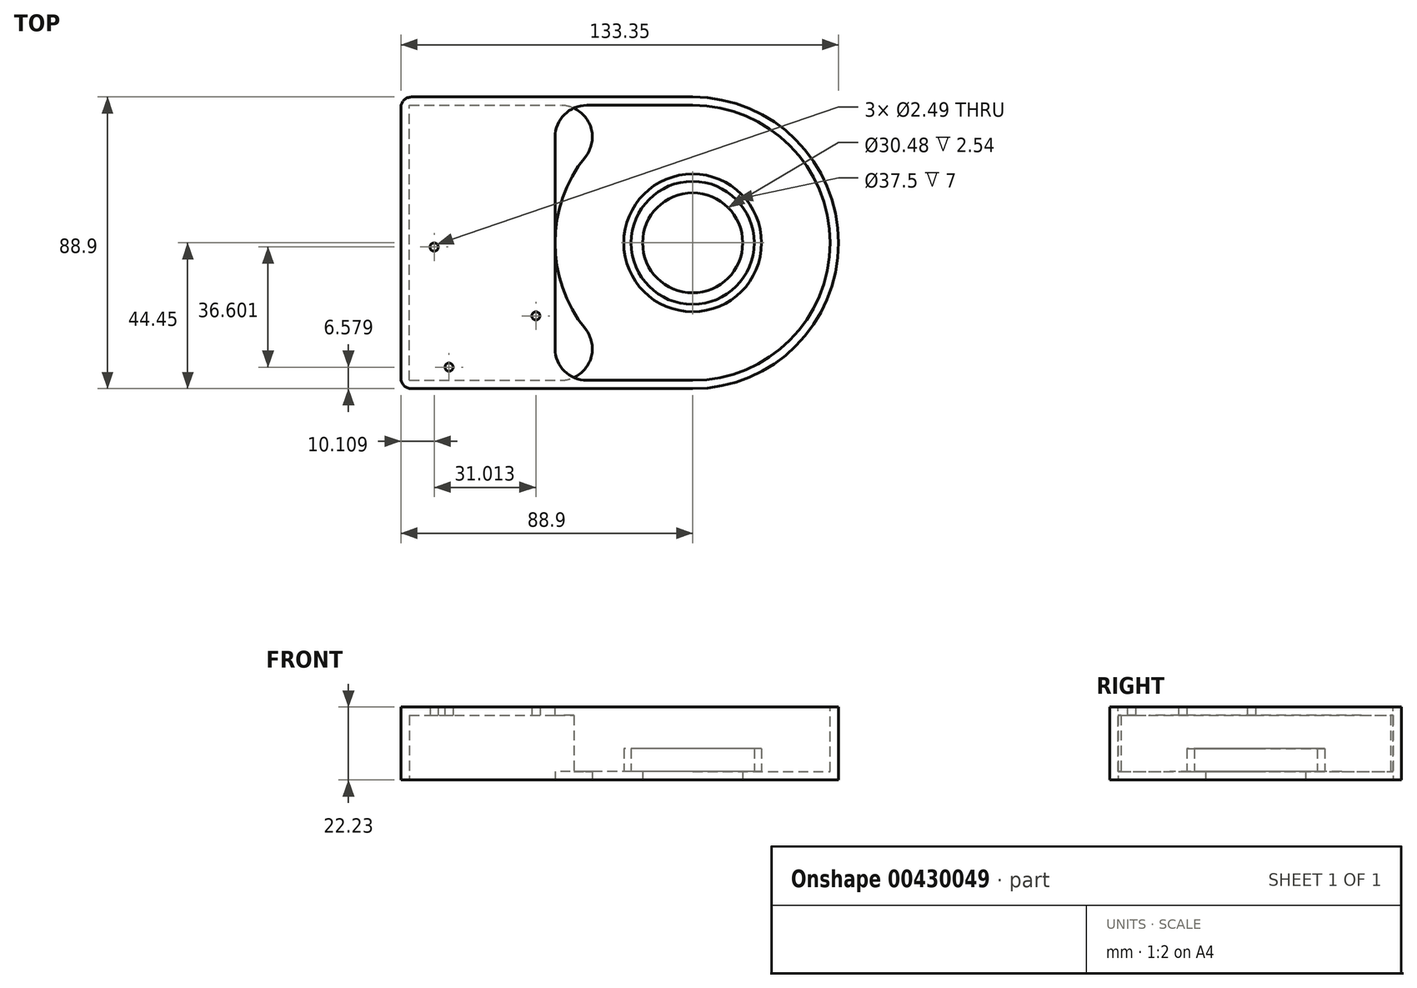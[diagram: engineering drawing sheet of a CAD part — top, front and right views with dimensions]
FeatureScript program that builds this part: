
annotation { "Feature Type Name" : "Feature", "Feature Type Description" : "" }
export const myFeature = defineFeature(function(context is Context, id is Id, definition is map)
    precondition{}
    {
        {
            var Q0;
            Q0=qCreatedBy(makeId("Top.planeOp"),FACE);
            var sketch = newSketch(context, id + "F0", { "sketchPlane" : qUnion([Q0])});
            skLineSegment(sketch, "E0.bottom", {"start": v(3.17, 0) * mm, "end": v(88.9, 0) * mm});
            skLineSegment(sketch, "E0.top", {"start": v(3.17, 88.9) * mm, "end": v(88.9, 88.9) * mm});
            skLineSegment(sketch, "E0.left", {"start": v(0, 3.17) * mm, "end": v(0, 85.73) * mm});
            skLineSegment(sketch, "E0.right", {"start": v(88.9, 0) * mm, "end": v(88.9, 88.9) * mm});
            skArc(sketch, "E1", {"start": v(88.9, 0) * mm, "mid": v(133.35, 44.45) * mm, "end": v(88.9, 88.9) * mm});
            skPoint(sketch, "E1.third.point", {"position": v(133.34, 45.55) * mm});
            skCircle(sketch, "E2", {"center": v(88.9, 44.45) * mm, "radius": 15.24 * mm});
            skPoint(sketch, "E3.visualSharp", {"position": v(0, 88.9) * mm});
            skArc(sketch, "E3.filletArc", {"start": v(3.17, 88.9) * mm, "mid": v(0.93, 87.97) * mm, "end": v(0, 85.73) * mm});
            skPoint(sketch, "E4.visualSharp", {"position": v(0, 0) * mm});
            skArc(sketch, "E4.filletArc", {"start": v(0, 3.17) * mm, "mid": v(0.93, 0.93) * mm, "end": v(3.17, 0) * mm});
            skSolve(sketch);
        }
        {
            var Q0;
            Q0=qSketchRegion(id+"F0",true);
            extrude(context, id + "F1", {"entities" : qUnion([Q0]), "depth" : 22.22 * mm});
        }
        {
            var Q0;
            Q0=makeQuery(id+"F1.opExtrude","CAP_FACE",FACE,{"disambiguationData":[OSD([sQuery(id+"F0.wireOp",EDGE,"E0.bottom"),sQuery(id+"F0.wireOp",EDGE,"E0.top"),sQuery(id+"F0.wireOp",EDGE,"E0.left"),sQuery(id+"F0.wireOp",EDGE,"E1"),sQuery(id+"F0.wireOp",EDGE,"E2")])],"isStart":false});
            var sketch = newSketch(context, id + "F2", { "sketchPlane" : qUnion([Q0])});
            skArc(sketch, "E5.0.0", {"start": v(88.9, 0) * mm, "mid": v(133.35, 44.45) * mm, "end": v(88.9, 88.9) * mm, "construction": true});
            skArc(sketch, "E6", {"start": v(88.9, 2.54) * mm, "mid": v(130.8, 44.45) * mm, "end": v(88.9, 86.36) * mm});
            skLineSegment(sketch, "E7.bottom", {"start": v(88.9, 86.36) * mm, "end": v(56.64, 86.36) * mm});
            skLineSegment(sketch, "E7.top", {"start": v(88.9, 2.54) * mm, "end": v(56.64, 2.54) * mm});
            skLineSegment(sketch, "E7.left", {"start": v(88.9, 86.36) * mm, "end": v(88.9, 2.54) * mm});
            skLineSegment(sketch, "E7.right", {"start": v(46.99, 76.7) * mm, "end": v(46.99, 12.2) * mm});
            skPoint(sketch, "E8.visualSharp", {"position": v(46.99, 86.36) * mm});
            skArc(sketch, "E8.filletArc", {"start": v(56.64, 86.36) * mm, "mid": v(49.82, 83.53) * mm, "end": v(46.99, 76.7) * mm});
            skPoint(sketch, "E9.visualSharp", {"position": v(47, 2.54) * mm});
            skArc(sketch, "E9.filletArc", {"start": v(46.99, 12.2) * mm, "mid": v(49.82, 5.37) * mm, "end": v(56.64, 2.54) * mm});
            skSolve(sketch);
        }
        {
            var Q0;
            Q0=qSketchRegion(id+"F2",true);
            extrude(context, id + "F3", {"entities" : qUnion([Q0]), "operationType" : NewBodyOperationType.REMOVE, "oppositeDirection" : true, "depth" : 19.68 * mm});
        }
        {
            var Q0;
            Q0=makeQuery(id+"F1.opExtrude","CAP_FACE",FACE,{"disambiguationData":[OSD([sQuery(id+"F0.wireOp",EDGE,"E0.bottom"),sQuery(id+"F0.wireOp",EDGE,"E0.top"),sQuery(id+"F0.wireOp",EDGE,"E0.left"),sQuery(id+"F0.wireOp",EDGE,"E1"),sQuery(id+"F0.wireOp",EDGE,"E2")])],"isStart":true});
            var sketch = newSketch(context, id + "F4", { "sketchPlane" : qUnion([Q0])});
            skArc(sketch, "E10", {"start": v(56.2, -18.23) * mm, "mid": v(46.99, -44.45) * mm, "end": v(56.2, -70.67) * mm});
            skLineSegment(sketch, "E11.0", {"start": v(2.54, -86.36) * mm, "end": v(48.67, -86.36) * mm});
            skLineSegment(sketch, "E11.1", {"start": v(2.54, -2.54) * mm, "end": v(2.54, -86.36) * mm});
            skLineSegment(sketch, "E11.2", {"start": v(2.54, -2.54) * mm, "end": v(48.67, -2.54) * mm});
            skPoint(sketch, "E12.visualSharp", {"position": v(88.9, -2.54) * mm});
            skArc(sketch, "E12.filletArc", {"start": v(56.2, -18.23) * mm, "mid": v(57.38, -8.02) * mm, "end": v(48.67, -2.54) * mm});
            skPoint(sketch, "E13.visualSharp", {"position": v(88.9, -86.36) * mm});
            skArc(sketch, "E13.filletArc", {"start": v(48.67, -86.36) * mm, "mid": v(57.38, -80.88) * mm, "end": v(56.2, -70.67) * mm});
            skSolve(sketch);
        }
        {
            var Q0;
            Q0=qSketchRegion(id+"F4",true);
            extrude(context, id + "F5", {"entities" : qUnion([Q0]), "operationType" : NewBodyOperationType.REMOVE, "oppositeDirection" : true, "depth" : 19.68 * mm});
        }
        {
            var Q0;
            Q0=makeQuery(id+"F3.boolean.opBoolean","COPY",FACE,{"derivedFrom":makeQuery(id+"F3.opExtrude","CAP_FACE",FACE,{"disambiguationData":[OSD([sQuery(id+"F2.wireOp",EDGE,"E6"),sQuery(id+"F2.wireOp",EDGE,"E7.bottom"),sQuery(id+"F2.wireOp",EDGE,"E7.top"),sQuery(id+"F2.wireOp",EDGE,"E7.right"),sQuery(id+"F2.wireOp",EDGE,"E8.filletArc"),sQuery(id+"F2.wireOp",EDGE,"E9.filletArc")])],"isStart":false})});
            var sketch = newSketch(context, id + "F6", { "sketchPlane" : qUnion([Q0])});
            skCircle(sketch, "E14", {"center": v(88.9, 44.45) * mm, "radius": 21 * mm});
            skCircle(sketch, "E15", {"center": v(88.9, 44.45) * mm, "radius": 18.75 * mm});
            skSolve(sketch);
        }
        {
            var Q0;
            Q0=qSketchRegion(id+"F6",true);
            extrude(context, id + "F7", {"entities" : qUnion([Q0]), "operationType" : NewBodyOperationType.ADD, "depth" : 7 * mm});
        }
        {
            var Q0;
            Q0=makeQuery(id+"F5.boolean.opBoolean","COPY",FACE,{"derivedFrom":makeQuery(id+"F5.opExtrude","CAP_FACE",FACE,{"disambiguationData":[OSD([sQuery(id+"F4.wireOp",EDGE,"E10"),sQuery(id+"F4.wireOp",EDGE,"E11.0"),sQuery(id+"F4.wireOp",EDGE,"E11.1"),sQuery(id+"F4.wireOp",EDGE,"E11.2"),sQuery(id+"F4.wireOp",EDGE,"E12.filletArc"),sQuery(id+"F4.wireOp",EDGE,"E13.filletArc")])],"isStart":false})});
            var sketch = newSketch(context, id + "F8", { "sketchPlane" : qUnion([Q0])});
            skCircle(sketch, "E16", {"center": v(10.1, -43.18) * mm, "radius": 1.24 * mm});
            skCircle(sketch, "E17", {"center": v(14.63, -6.58) * mm, "radius": 1.24 * mm});
            skCircle(sketch, "E18", {"center": v(41.12, -22.2) * mm, "radius": 1.24 * mm});
            skSolve(sketch);
        }
        {
            var Q0;
            Q0=qSketchRegion(id+"F8",true);
            extrude(context, id + "F9", {"entities" : qUnion([Q0]), "operationType" : NewBodyOperationType.REMOVE, "endBound" : BoundingType.THROUGH_ALL, "oppositeDirection" : true, "depth" : 25.4 * mm});
        }
    });
